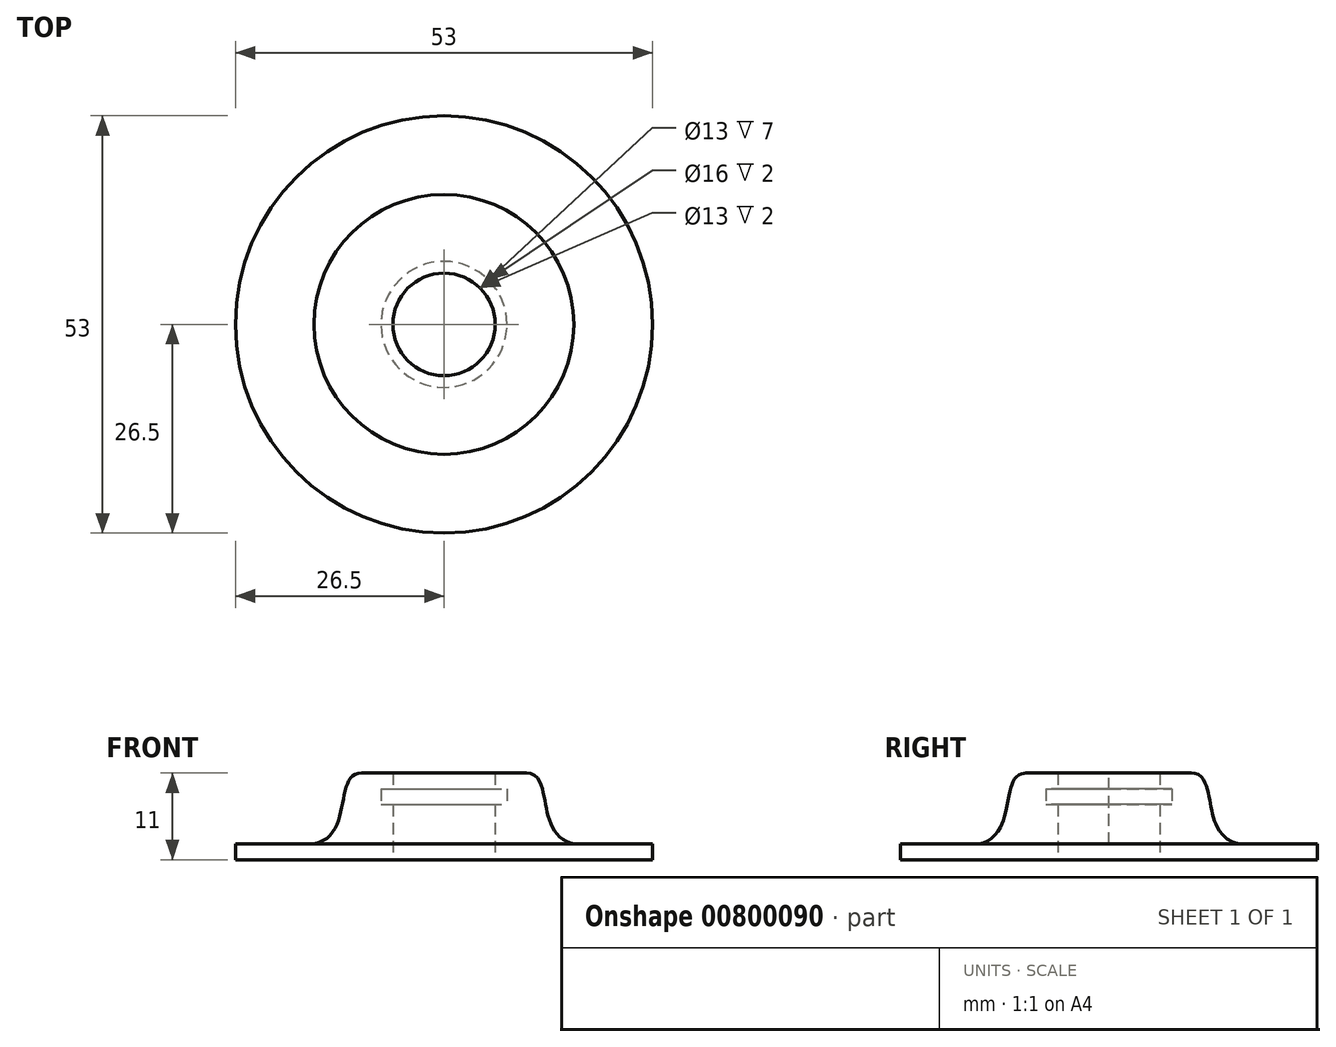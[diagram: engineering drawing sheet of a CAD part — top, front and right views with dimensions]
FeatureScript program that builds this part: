
annotation { "Feature Type Name" : "Feature", "Feature Type Description" : "" }
export const myFeature = defineFeature(function(context is Context, id is Id, definition is map)
    precondition{}
    {
        {
            var Q0;
            Q0=qCreatedBy(makeId("Front.planeOp"),FACE);
            var sketch = newSketch(context, id + "F0", { "sketchPlane" : qUnion([Q0])});
            skLineSegment(sketch, "E0.bottom", {"start": v(-6.5, 0) * mm, "end": v(-16.5, 0) * mm});
            skLineSegment(sketch, "E0.top", {"start": v(-6.5, 2) * mm, "end": v(-16.5, 2) * mm});
            skLineSegment(sketch, "E0.left", {"start": v(-6.5, 0) * mm, "end": v(-6.5, 2) * mm});
            skLineSegment(sketch, "E0.right", {"start": v(-16.5, 0) * mm, "end": v(-16.5, 2) * mm});
            skLineSegment(sketch, "E1.bottom", {"start": v(-6.5, 2) * mm, "end": v(-10.5, 2) * mm});
            skLineSegment(sketch, "E1.top", {"start": v(-6.5, 7) * mm, "end": v(-10.5, 7) * mm});
            skLineSegment(sketch, "E1.left", {"start": v(-6.5, 2) * mm, "end": v(-6.5, 7) * mm});
            skLineSegment(sketch, "E1.right", {"start": v(-10.5, 2) * mm, "end": v(-10.5, 7) * mm});
            skLineSegment(sketch, "E2.bottom", {"start": v(-10.5, 7) * mm, "end": v(-8, 7) * mm});
            skLineSegment(sketch, "E2.top", {"start": v(-10.5, 9) * mm, "end": v(-8, 9) * mm});
            skLineSegment(sketch, "E2.left", {"start": v(-10.5, 7) * mm, "end": v(-10.5, 9) * mm});
            skLineSegment(sketch, "E2.right", {"start": v(-8, 7) * mm, "end": v(-8, 9) * mm});
            skLineSegment(sketch, "E3.bottom", {"start": v(-10.5, 9) * mm, "end": v(-6.5, 9) * mm});
            skLineSegment(sketch, "E3.top", {"start": v(-10.5, 11) * mm, "end": v(-6.5, 11) * mm});
            skLineSegment(sketch, "E3.left", {"start": v(-10.5, 9) * mm, "end": v(-10.5, 11) * mm});
            skLineSegment(sketch, "E3.right", {"start": v(-6.5, 9) * mm, "end": v(-6.5, 11) * mm});
            skLineSegment(sketch, "E4.bottom", {"start": v(-6.5, 11) * mm, "end": v(-8.5, 11) * mm});
            skFitSpline(sketch, "E5", {"points": [v(-16.5, 2) * mm, v(-10.5, 11) * mm], "startDerivative": vector(15.3, 3.23) * mm, "endDerivative": vector(10.75, -0.04) * mm});
            skLineSegment(sketch, "E6.bottom", {"start": v(-16.5, 0) * mm, "end": v(-26.5, 0) * mm});
            skLineSegment(sketch, "E6.top", {"start": v(-16.5, 2) * mm, "end": v(-26.5, 2) * mm});
            skLineSegment(sketch, "E6.right", {"start": v(-26.5, 0) * mm, "end": v(-26.5, 2) * mm});
            skPoint(sketch, "E7", {"position": v(0, 12.56) * mm});
            skLineSegment(sketch, "E8", {"start": v(0, 0) * mm, "end": v(0, 12.56) * mm});
            skSolve(sketch);
        }
        {
            var Q0;
            Q0 = qSketchRegion(id + "F0", true);
            var Q1;
            Q1=sQuery(id+"F0.wireOp",EDGE,"E8");
            revolve(context, id + "F1", {"surfaceOperationType" : NewSurfaceOperationType.NEW, "entities" : qUnion([Q0]), "axis" : qUnion([Q1]), "revolveType" : RevolveType.FULL});
        }
    });
